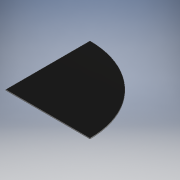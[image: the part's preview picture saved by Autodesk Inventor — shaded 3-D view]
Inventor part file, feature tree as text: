
AUTODESK INVENTOR PART (.ipt)
format: ipt  version: 2016 (Build 200138000, 138)  size: 107,520 bytes
history: native  units: mm
features: extrude x1, sketch x1
ambient origin geometry x8: Origin, YZ Plane, XZ Plane, XY Plane, X Axis, Y Axis, Z Axis, Center Point
bodies: 实体1 (feature_tree)
feature tree (2):
  extrude  "拉伸1"  Depth=500.0mm
  sketch  "草图1"  dims[d0=500.0mm d1=500.0mm d2=90.0deg d3=500.0mm d4=5.0mm d5=0.0mm]
